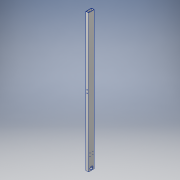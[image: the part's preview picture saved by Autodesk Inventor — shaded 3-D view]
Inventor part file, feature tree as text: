
AUTODESK INVENTOR PART (.ipt)
format: ipt  version: 2017 (Build 210142000, 142)  size: 149,504 bytes
history: native  units: in
note: dims shown in document units (in); Inventor stores cm internally (conversion verified against a paired STEP export)
features: sketch x5, extrude x3, hole x2
ambient origin geometry x8: Origin, YZ Plane, XZ Plane, XY Plane, X Axis, Y Axis, Z Axis, Center Point
bodies: Solid1 (feature_tree)
feature tree (10):
  extrude  "Extrusion1"  Depth=2.0in
  extrude  "Extrusion2"  Depth=1.75in
  extrude  "Extrusion3"  Depth=0.125in
  hole  "Hole1"  [1 undecoded]
  hole  "Hole2"  [1 undecoded]
  sketch  "Sketch2"  dims[d2=1.0in d3=2.0in]
  sketch  "Sketch3"  dims[d4=0.75in d5=1.75in]
  sketch  "Sketch4"  dims[d6=0.125in d7=0.125in]
  sketch  "Sketch5"  dims[d8=48.0in d9=0.0in d10=48.0in]
  sketch  "Sketch6"  dims[d11=24.0in d12=0.5in d13=0.25in d14=48.0in d15=0.0in d16=1.125in d17=1.125in d18=0.25in d19=0.0in d20=4.5in d21=0.5in d22=0.125in d24=0.125in d25=0.75in d26=0.375in d27=0.25in d28=0.5635in d29=0.125in d30=0.8108in d31=0.4375in d32=0.4375in d33=0.75in d34=1.125in d35=0.75in d36=0.375in d37=0.25in d38=0.5635in d39=0.125in d40=0.8108in]
note: 2 required parameter values undecoded (feature->parameter linkage not recoverable at this tier; creation-order binding heuristic only, values carry confidence <= 0.55)
